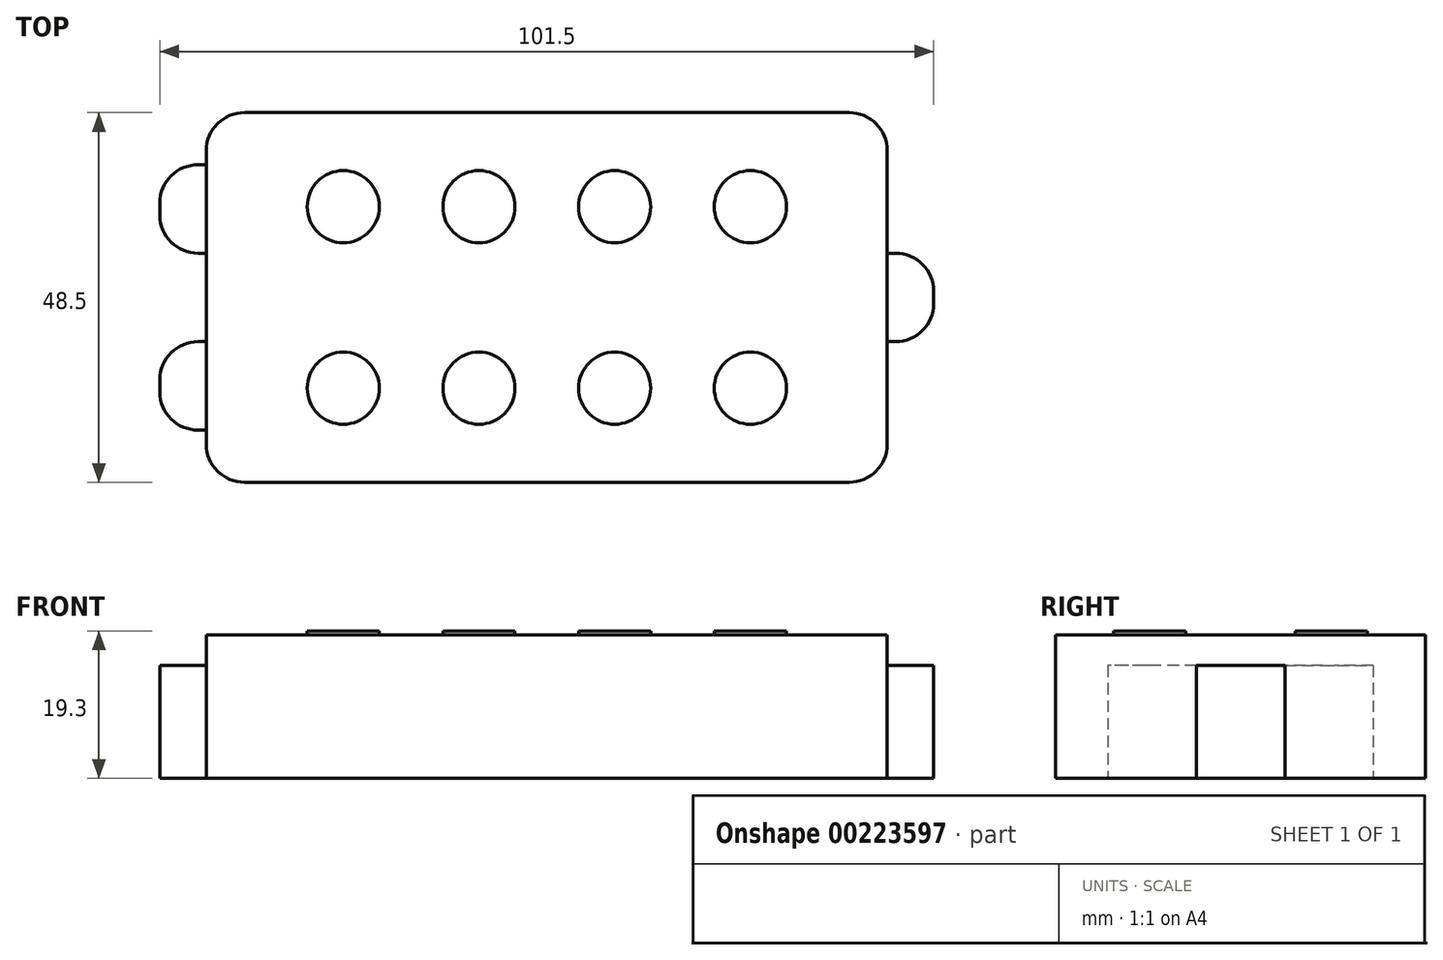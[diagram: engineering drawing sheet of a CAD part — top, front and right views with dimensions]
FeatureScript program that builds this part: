
annotation { "Feature Type Name" : "Feature", "Feature Type Description" : "" }
export const myFeature = defineFeature(function(context is Context, id is Id, definition is map)
    precondition{}
    {
        {
            var Q0;
            Q0=qCreatedBy(makeId("Top.planeOp"),FACE);
            var sketch = newSketch(context, id + "F0", { "sketchPlane" : qUnion([Q0])});
            skLineSegment(sketch, "E0", {"start": v(-44.66, 24.25) * mm, "end": v(44.65, 24.25) * mm});
            skLineSegment(sketch, "E1", {"start": v(44.66, 24.25) * mm, "end": v(44.66, -24.25) * mm});
            skLineSegment(sketch, "E2", {"start": v(-44.66, 24.25) * mm, "end": v(-44.66, -24.25) * mm});
            skLineSegment(sketch, "E3", {"start": v(-44.66, -24.25) * mm, "end": v(44.66, -24.25) * mm});
            skSolve(sketch);
        }
        {
            var Q0;
            Q0=makeQuery(id+"F0.imprint","IMPRINT",FACE,{"disambiguationData":[TD([[makeQuery(id+"F0.imprint","IMPRINT",EDGE,{"derivedFrom":sQuery(id+"F0.wireOp",EDGE,"E0")}),-1.0]])]});
            extrude(context, id + "F1", {"entities" : qUnion([Q0]), "depth" : 18.8 * mm});
        }
        {
            var Q0;
            Q0=makeQuery(id+"F1.opExtrude","CAP_FACE",FACE,{"disambiguationData":[OSD([sQuery(id+"F0.wireOp",EDGE,"E0"),sQuery(id+"F0.wireOp",EDGE,"E1"),sQuery(id+"F0.wireOp",EDGE,"E2"),sQuery(id+"F0.wireOp",EDGE,"E3")])],"isStart":false});
            var sketch = newSketch(context, id + "F2", { "sketchPlane" : qUnion([Q0])});
            skLineSegment(sketch, "E4", {"start": v(-26.7, 30.79) * mm, "end": v(-26.7, -32.54) * mm, "construction": true});
            skLineSegment(sketch, "E5", {"start": v(-51.97, 11.9) * mm, "end": v(52.62, 11.9) * mm, "construction": true});
            skLineSegment(sketch, "E6", {"start": v(-50.25, -11.9) * mm, "end": v(52.93, -11.9) * mm, "construction": true});
            skCircle(sketch, "E7", {"center": v(-26.7, 11.9) * mm, "radius": 4.73 * mm});
            skCircle(sketch, "E8.0.1.0", {"center": v(-26.7, -11.9) * mm, "radius": 4.73 * mm});
            skCircle(sketch, "E8.1.0.0", {"center": v(-8.9, 11.9) * mm, "radius": 4.73 * mm});
            skCircle(sketch, "E8.1.1.0", {"center": v(-8.9, -11.9) * mm, "radius": 4.73 * mm});
            skCircle(sketch, "E8.2.0.0", {"center": v(8.9, 11.9) * mm, "radius": 4.73 * mm});
            skCircle(sketch, "E8.2.1.0", {"center": v(8.9, -11.9) * mm, "radius": 4.73 * mm});
            skCircle(sketch, "E8.3.0.0", {"center": v(26.7, 11.9) * mm, "radius": 4.73 * mm});
            skCircle(sketch, "E8.3.1.0", {"center": v(26.7, -11.9) * mm, "radius": 4.73 * mm});
            skLineSegment(sketch, "E8.direction1", {"start": v(-26.7, 11.9) * mm, "end": v(-8.9, 11.9) * mm, "construction": true});
            skLineSegment(sketch, "E8.direction2", {"start": v(-26.7, 11.9) * mm, "end": v(-26.7, -11.9) * mm, "construction": true});
            skSolve(sketch);
        }
        {
            var Q0;
            Q0 = qSketchRegion(id + "F2", true);
            extrude(context, id + "F3", {"entities" : qUnion([Q0]), "operationType" : NewBodyOperationType.ADD, "depth" : .5 * mm});
        }
        {
            var Q0;
            Q0=makeQuery(id+"F1.opExtrude","SWEPT_EDGE",EDGE,{"disambiguationData":[OSD([sQuery(id+"F0.wireOp",EDGE,"E0"),sQuery(id+"F0.wireOp",EDGE,"E2")])]});
            var Q1;
            Q1=makeQuery(id+"F1.opExtrude","SWEPT_EDGE",EDGE,{"disambiguationData":[OSD([sQuery(id+"F0.wireOp",EDGE,"E2"),sQuery(id+"F0.wireOp",EDGE,"E3")])]});
            var Q2;
            Q2=makeQuery(id+"F1.opExtrude","SWEPT_EDGE",EDGE,{"disambiguationData":[OSD([sQuery(id+"F0.wireOp",EDGE,"E1"),sQuery(id+"F0.wireOp",EDGE,"E3")])]});
            var Q3;
            Q3=makeQuery(id+"F1.opExtrude","SWEPT_EDGE",EDGE,{"disambiguationData":[OSD([sQuery(id+"F0.wireOp",EDGE,"E0"),sQuery(id+"F0.wireOp",EDGE,"E1")])]});
            fillet(context, id + "F4", {"entities" : qUnion([Q0, Q1, Q2, Q3]), "radius" : 5 * mm, "tangentPropagation" : true, "allowEdgeOverflow" : false});
        }
        {
            var Q0;
            Q0=qCreatedBy(makeId("Top.planeOp"),FACE);
            var sketch = newSketch(context, id + "F5", { "sketchPlane" : qUnion([Q0])});
            skLineSegment(sketch, "E9", {"start": v(44.66, 5.8) * mm, "end": v(45.75, 5.8) * mm});
            skLineSegment(sketch, "E10.0", {"start": v(44.66, 5.8) * mm, "end": v(44.66, -5.8) * mm});
            skLineSegment(sketch, "E11", {"start": v(44.66, -5.8) * mm, "end": v(45.75, -5.8) * mm});
            skLineSegment(sketch, "E12", {"start": v(50.75, 0.8) * mm, "end": v(50.75, -0.8) * mm});
            skArc(sketch, "E13.filletArc", {"start": v(50.75, 0.8) * mm, "mid": v(49.29, 4.34) * mm, "end": v(45.75, 5.8) * mm});
            skArc(sketch, "E14.filletArc", {"start": v(45.75, -5.8) * mm, "mid": v(49.29, -4.34) * mm, "end": v(50.75, -0.8) * mm});
            skSolve(sketch);
        }
        {
            var Q0;
            Q0 = qSketchRegion(id + "F5", true);
            extrude(context, id + "F6", {"entities" : qUnion([Q0]), "operationType" : NewBodyOperationType.ADD, "depth" : 14.78 * mm});
        }
        {
            var Q0;
            Q0=qCreatedBy(makeId("Top.planeOp"),FACE);
            var sketch = newSketch(context, id + "F7", { "sketchPlane" : qUnion([Q0])});
            skLineSegment(sketch, "E15.MirrorCS", {"start": v(-45.75, 5.8) * mm, "end": v(-44.66, 5.8) * mm});
            skLineSegment(sketch, "E16", {"start": v(-44.66, 5.8) * mm, "end": v(-44.66, 17.4) * mm});
            skLineSegment(sketch, "E17", {"start": v(-50.75, 10.8) * mm, "end": v(-50.75, 12.4) * mm});
            skLineSegment(sketch, "E18", {"start": v(-44.66, 17.4) * mm, "end": v(-45.75, 17.4) * mm});
            skPoint(sketch, "E19.newPointA", {"position": v(-45.75, 17.4) * mm});
            skArc(sketch, "E19.filletArc", {"start": v(-45.75, 17.4) * mm, "mid": v(-49.29, 15.94) * mm, "end": v(-50.75, 12.4) * mm});
            skPoint(sketch, "E20.newPointA", {"position": v(-45.75, 5.8) * mm});
            skArc(sketch, "E20.filletArc", {"start": v(-50.75, 10.8) * mm, "mid": v(-49.29, 7.26) * mm, "end": v(-45.75, 5.8) * mm});
            skLineSegment(sketch, "E21.MirrorCS", {"start": v(-44.66, -17.4) * mm, "end": v(-45.75, -17.4) * mm});
            skLineSegment(sketch, "E22.MirrorCS", {"start": v(-45.75, -5.8) * mm, "end": v(-44.66, -5.8) * mm});
            skArc(sketch, "E23.MirrorCS", {"start": v(-50.75, -10.8) * mm, "mid": v(-49.29, -7.26) * mm, "end": v(-45.75, -5.8) * mm});
            skPoint(sketch, "E24.MirrorP", {"position": v(-45.75, -5.8) * mm});
            skLineSegment(sketch, "E25.MirrorCS", {"start": v(-44.66, -5.8) * mm, "end": v(-44.66, -17.4) * mm});
            skLineSegment(sketch, "E26.MirrorCS", {"start": v(-50.75, -10.8) * mm, "end": v(-50.75, -12.4) * mm});
            skPoint(sketch, "E27.MirrorP", {"position": v(-45.75, -17.4) * mm});
            skArc(sketch, "E28.MirrorCS", {"start": v(-45.75, -17.4) * mm, "mid": v(-49.29, -15.94) * mm, "end": v(-50.75, -12.4) * mm});
            skSolve(sketch);
        }
        {
            var Q0;
            Q0 = qSketchRegion(id + "F7", true);
            extrude(context, id + "F8", {"entities" : qUnion([Q0]), "operationType" : NewBodyOperationType.ADD, "depth" : 14.78 * mm});
        }
    });
